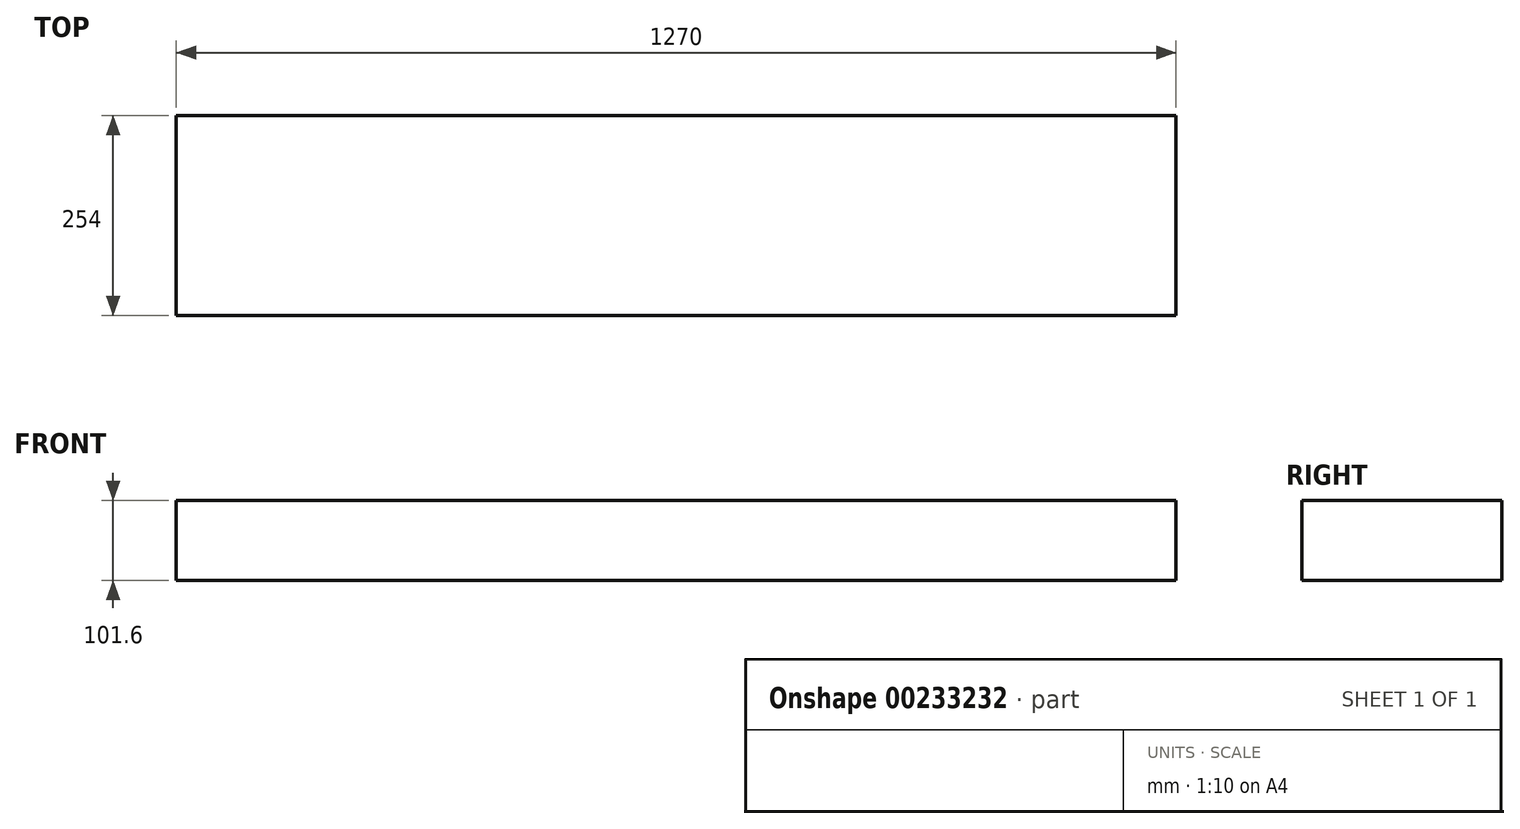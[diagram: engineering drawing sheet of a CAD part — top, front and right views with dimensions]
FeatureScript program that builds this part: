
annotation { "Feature Type Name" : "Feature", "Feature Type Description" : "" }
export const myFeature = defineFeature(function(context is Context, id is Id, definition is map)
    precondition{}
    {
        {
            var Q0;
            Q0=qCreatedBy(makeId("Top.planeOp"),FACE);
            var sketch = newSketch(context, id + "F0", { "sketchPlane" : qUnion([Q0])});
            skLineSegment(sketch, "E0.bottom", {"start": v(-1374.83, -1272.97) * mm, "end": v(-104.83, -1272.97) * mm});
            skLineSegment(sketch, "E0.top", {"start": v(-1374.83, -1018.97) * mm, "end": v(-104.83, -1018.97) * mm});
            skLineSegment(sketch, "E0.left", {"start": v(-1374.83, -1272.97) * mm, "end": v(-1374.83, -1018.97) * mm});
            skLineSegment(sketch, "E0.right", {"start": v(-104.83, -1272.97) * mm, "end": v(-104.83, -1018.97) * mm});
            skSolve(sketch);
        }
        {
            var Q0;
            Q0=makeQuery(id+"F0.imprint","IMPRINT",FACE,{"disambiguationData":[TD([[makeQuery(id+"F0.imprint","IMPRINT",EDGE,{"derivedFrom":sQuery(id+"F0.wireOp",EDGE,"E0.bottom")}),1.0]])]});
            extrude(context, id + "F1", {"entities" : qUnion([Q0]), "depth" : 101.6 * mm});
        }
    });
